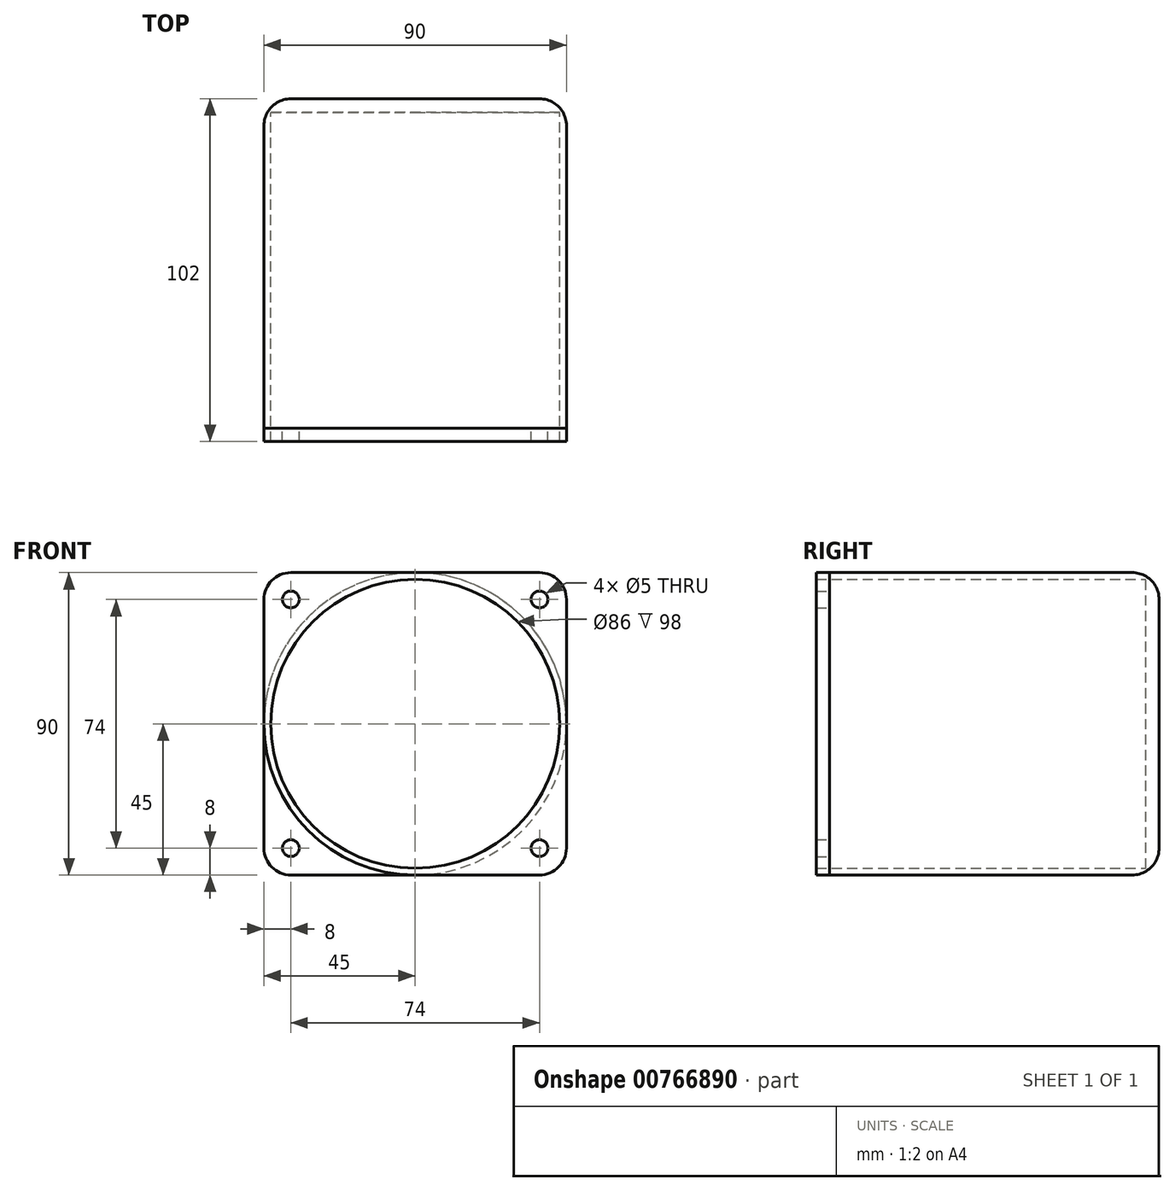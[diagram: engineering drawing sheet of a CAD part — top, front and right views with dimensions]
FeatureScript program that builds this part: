
annotation { "Feature Type Name" : "Feature", "Feature Type Description" : "" }
export const myFeature = defineFeature(function(context is Context, id is Id, definition is map)
    precondition{}
    {
        {
            var Q0;
            Q0=qCreatedBy(makeId("Front.planeOp"),FACE);
            var sketch = newSketch(context, id + "F0", { "sketchPlane" : qUnion([Q0])});
            skLineSegment(sketch, "E0.bottom", {"start": v(-45, -45) * mm, "end": v(45, -45) * mm});
            skLineSegment(sketch, "E0.top", {"start": v(-45, 45) * mm, "end": v(45, 45) * mm});
            skLineSegment(sketch, "E0.left", {"start": v(-45, -45) * mm, "end": v(-45, 45) * mm});
            skLineSegment(sketch, "E0.right", {"start": v(45, -45) * mm, "end": v(45, 45) * mm});
            skCircle(sketch, "E1", {"center": v(0, 0) * mm, "radius": 45 * mm});
            skCircle(sketch, "E2", {"center": v(0, 0) * mm, "radius": 43 * mm});
            skCircle(sketch, "E3", {"center": v(-37, 37) * mm, "radius": 2.5 * mm});
            skCircle(sketch, "E4", {"center": v(-37, -37) * mm, "radius": 2.5 * mm});
            skCircle(sketch, "E5", {"center": v(37, -37) * mm, "radius": 2.5 * mm});
            skCircle(sketch, "E6", {"center": v(37, 37) * mm, "radius": 2.5 * mm});
            skSolve(sketch);
        }
        {
            var Q0;
            {var subQ0=sQuery(id+"F0.wireOp",EDGE,"E0.right");var subQ1=sQuery(id+"F0.wireOp",EDGE,"E0.top");var subQ2=makeQuery(id+"F0.imprint","INTERSECT",VERTEX,{"derivedFrom":[subQ1,subQ0]});Q0=makeQuery(id+"F0.imprint","IMPRINT",FACE,{"disambiguationData":[TD([[makeQuery(id+"F0.imprint","IMPRINT",EDGE,{"disambiguationData":[TD([[subQ2,1.0]])],"derivedFrom":subQ1}),-1.0]])]});}
            var Q1;
            {var subQ0=sQuery(id+"F0.wireOp",EDGE,"E0.left");var subQ1=sQuery(id+"F0.wireOp",EDGE,"E0.top");var subQ2=makeQuery(id+"F0.imprint","INTERSECT",VERTEX,{"derivedFrom":[subQ1,subQ0]});Q1=makeQuery(id+"F0.imprint","IMPRINT",FACE,{"disambiguationData":[TD([[makeQuery(id+"F0.imprint","IMPRINT",EDGE,{"disambiguationData":[TD([[subQ2,-1.0]])],"derivedFrom":subQ1}),-1.0]])]});}
            var Q2;
            {var subQ0=sQuery(id+"F0.wireOp",EDGE,"E0.left");var subQ1=sQuery(id+"F0.wireOp",EDGE,"E0.bottom");var subQ2=makeQuery(id+"F0.imprint","INTERSECT",VERTEX,{"derivedFrom":[subQ1,subQ0]});Q2=makeQuery(id+"F0.imprint","IMPRINT",FACE,{"disambiguationData":[TD([[makeQuery(id+"F0.imprint","IMPRINT",EDGE,{"disambiguationData":[TD([[subQ2,-1.0]])],"derivedFrom":subQ1}),1.0]])]});}
            var Q3;
            {var subQ0=sQuery(id+"F0.wireOp",EDGE,"E0.right");var subQ1=sQuery(id+"F0.wireOp",EDGE,"E0.bottom");var subQ2=makeQuery(id+"F0.imprint","INTERSECT",VERTEX,{"derivedFrom":[subQ1,subQ0]});Q3=makeQuery(id+"F0.imprint","IMPRINT",FACE,{"disambiguationData":[TD([[makeQuery(id+"F0.imprint","IMPRINT",EDGE,{"disambiguationData":[TD([[subQ2,1.0]])],"derivedFrom":subQ1}),1.0]])]});}
            var Q4;
            Q4=makeQuery(id+"F0.imprint","IMPRINT",FACE,{"disambiguationData":[TD([[makeQuery(id+"F0.imprint","IMPRINT",EDGE,{"derivedFrom":sQuery(id+"F0.wireOp",EDGE,"E2")}),-1.0]])]});
            extrude(context, id + "F1", {"entities" : qUnion([Q0, Q1, Q2, Q3, Q4]), "depth" : 4 * mm, "offsetDistance" : 25 * mm});
        }
        {
            var Q0;
            Q0=makeQuery(id+"F0.imprint","IMPRINT",FACE,{"disambiguationData":[TD([[makeQuery(id+"F0.imprint","IMPRINT",EDGE,{"derivedFrom":sQuery(id+"F0.wireOp",EDGE,"E2")}),-1.0]])]});
            var Q1;
            Q1=makeQuery(id+"F0.imprint","IMPRINT",FACE,{"disambiguationData":[TD([[makeQuery(id+"F0.imprint","IMPRINT",EDGE,{"derivedFrom":sQuery(id+"F0.wireOp",EDGE,"E2")}),1.0]])]});
            extrude(context, id + "F2", {"entities" : qUnion([Q0, Q1]), "operationType" : NewBodyOperationType.ADD, "oppositeDirection" : true, "depth" : 98 * mm, "offsetDistance" : 25 * mm});
        }
        {
            var Q0;
            Q0=makeQuery(id+"F0.imprint","IMPRINT",FACE,{"disambiguationData":[TD([[makeQuery(id+"F0.imprint","IMPRINT",EDGE,{"derivedFrom":sQuery(id+"F0.wireOp",EDGE,"E2")}),1.0]])]});
            extrude(context, id + "F3", {"entities" : qUnion([Q0]), "operationType" : NewBodyOperationType.REMOVE, "oppositeDirection" : true, "depth" : 94 * mm, "offsetDistance" : 25 * mm});
        }
        {
            var Q0;
            Q0=makeQuery(id+"F2.opExtrude","CAP_EDGE",EDGE,{"disambiguationData":[OSD([sQuery(id+"F0.wireOp",EDGE,"E1")])],"isStart":false});
            var Q1;
            Q1=makeQuery(id+"F1.opExtrude","SWEPT_EDGE",EDGE,{"disambiguationData":[OSD([sQuery(id+"F0.wireOp",EDGE,"E0.top"),sQuery(id+"F0.wireOp",EDGE,"E0.right")])]});
            var Q2;
            Q2=makeQuery(id+"F1.opExtrude","SWEPT_EDGE",EDGE,{"disambiguationData":[OSD([sQuery(id+"F0.wireOp",EDGE,"E0.bottom"),sQuery(id+"F0.wireOp",EDGE,"E0.right")])]});
            var Q3;
            Q3=makeQuery(id+"F1.opExtrude","SWEPT_EDGE",EDGE,{"disambiguationData":[OSD([sQuery(id+"F0.wireOp",EDGE,"E0.bottom"),sQuery(id+"F0.wireOp",EDGE,"E0.left")])]});
            var Q4;
            Q4=makeQuery(id+"F1.opExtrude","SWEPT_EDGE",EDGE,{"disambiguationData":[OSD([sQuery(id+"F0.wireOp",EDGE,"E0.top"),sQuery(id+"F0.wireOp",EDGE,"E0.left")])]});
            fillet(context, id + "F4", {"entities" : qUnion([Q0, Q1, Q2, Q3, Q4]), "radius" : 8 * mm, "tangentPropagation" : true, "allowEdgeOverflow" : false});
        }
    });
